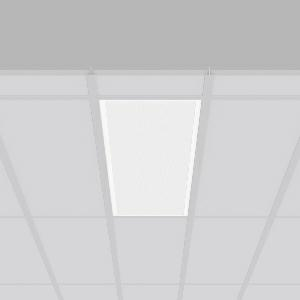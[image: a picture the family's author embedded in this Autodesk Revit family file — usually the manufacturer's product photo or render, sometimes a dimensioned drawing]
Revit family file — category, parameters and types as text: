
# Revit family: sidelite_eco_672367_002_1_89_2f6b
name_source: partatom
category: Lighting Fixtures
units: mm (PartAtom-declared; Revit-internal decimal feet)

## family parameters
Cut with Voids When Loaded = No
Host = Face
Light Source = No
Part Type = Normal
Room Calculation Point = No
Round Connector Dimension = Use Diameter
Shared = No

## types (1)
- SIDELITE ECO (1 x LED Modul 840, 3450 lm, 4000)
    Apparent Load = 30 VA
    CIE Flux Codes = 59 87 97 100 100
    Color Rendering = 80
    Color Temperature = 4000
    Default Elevation = 1800 mm
    Description = Series: SIDELITE ECO
Highly economical recessed luminaire with progressive LED technology. For escape route illumination. Frame made of aluminium, powder-coated. Diffuser plastic microprismatic. Lightguide and diffuser made of non-yellowing plastic (PMMA). Lateral light emission (RZB SIDELITE technology) for homogeneous light distribution. External driver. Second cable inlet for loop through. External driver with simple plug-in locking system. Extended connection cable (1.90 m). With AC Control monitoring module for LUXIFAIR central battery units. Luminaire can be used with accessories (to be ordered separately) for recessed, surface mounting or as pendant luminaire. 
Colour: white
Length: 1195 mm
Width: 295 mm
Cut-out length: 1170 mm
Cut-out width: 270 mm
Recess height: 160 mm
Luminaire: recess height: 40 mm
Weight: 3.94 kg
Operating mode: maintained power mode
Lamp: LED
Socket: without socket
Colour temperature: 4000K
Colour rendering index (CRI): 80
System power: 30 W
Rated luminous flux: 3450 lm
Luminous flux, emergency: 3450 lm
System power, emergency: 30 W
Control gear: Regulated power supply
Protection class: I
Type of protection: IP 20
    Height = 0 mm  [stored 0 ft]
    Lamp = 1 x LED Modul 840
    Lamp Light Flux = 3450 lm
    Lamp count = 1
    Length = 1195 mm
    Lifetime = 50000 h
    Luminous efficacy = 115 lm/W
    Manufacturer = RZB
    ModVariant = No
    Model = 672367.002.1.89
    Mounting Place = Ceiling
    Mounting Type = Recessed
    Number of Poles = 1
    OnlyDefault = Yes
    Power Factor = 1
    Product Name = SIDELITE ECO
    Product group = Recessed modular luminaires
    ProductGroupID = 406
    Protection Class = Protection class I
    Protection Degree = Degree of protection
    RLX_Detail_Level = 1
    RLX_Emergency_Light_Flux = 3450 lm
    RLX_Emergency_Type = 3
    RLX_Emergency_Type_DB = Yes
    RlxData = <blob elided: 35245 chars, md5=4c7a410a>
    Socket = socket
    Standby Power = 0 W
    System Light Flux = 3450 lm
    System Power = 30 W
    Type Comments = Product without accessories
    Type Image = 312366.002.jpg
    URL = http://relux.com
    VarID = ---
    Voltage = 0 V
    Weight = 0.00 kg
    Width = 295 mm

note: [stored X ft] marks values corroborated as IEEE doubles in the binary element streams (Revit-internal decimal feet)

## geometry (parser evidence)
native form markers: Blend x4, Sweep x11
no freeform markers — native parametric forms only
